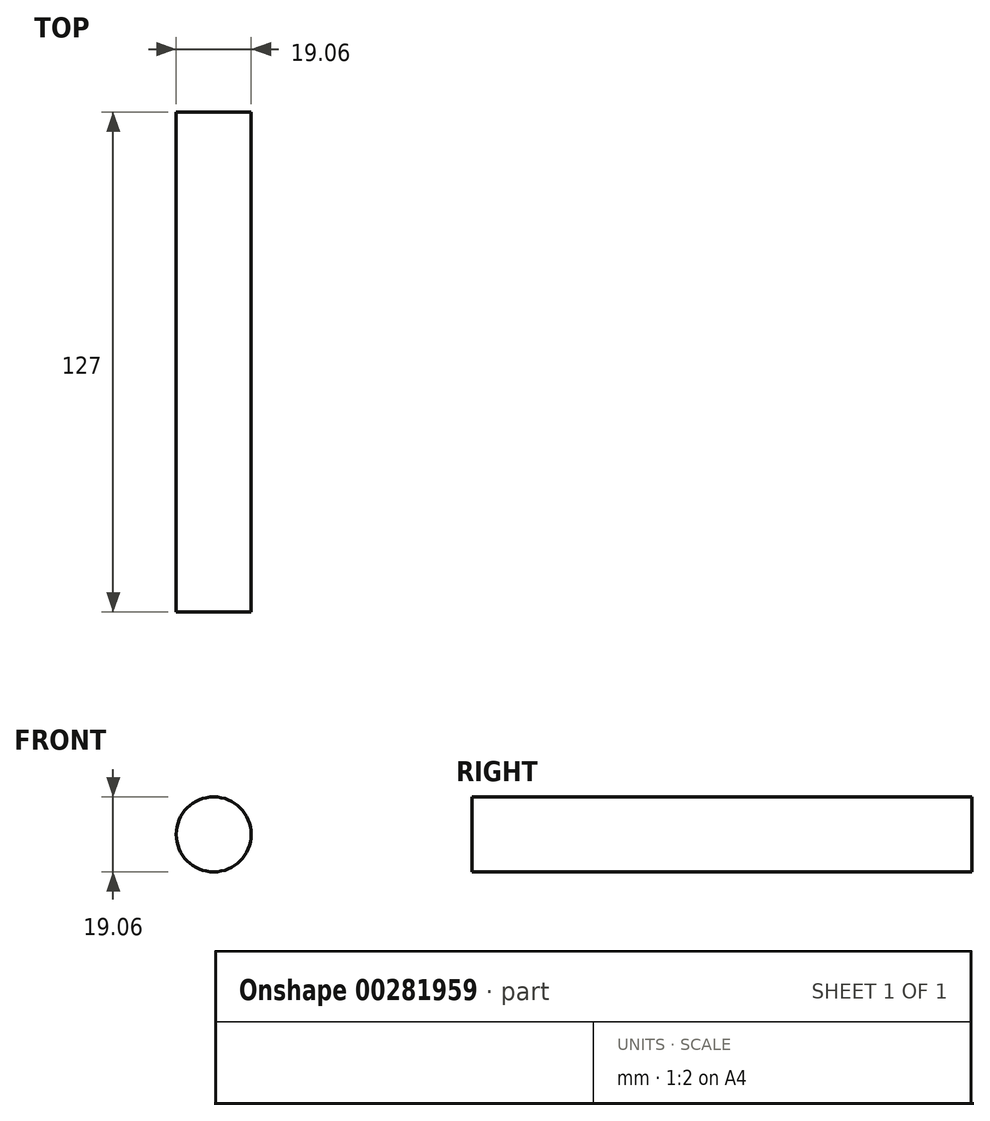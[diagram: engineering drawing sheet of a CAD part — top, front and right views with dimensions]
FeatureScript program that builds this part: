
annotation { "Feature Type Name" : "Feature", "Feature Type Description" : "" }
export const myFeature = defineFeature(function(context is Context, id is Id, definition is map)
    precondition{}
    {
        {
            var Q0;
            Q0=qCreatedBy(makeId("Front.planeOp"),FACE);
            var sketch = newSketch(context, id + "F0", { "sketchPlane" : qUnion([Q0])});
            skCircle(sketch, "E0", {"center": v(0, 0) * mm, "radius": 9.53 * mm});
            skSolve(sketch);
        }
        {
            var Q0;
            Q0=makeQuery(id+"F0.imprint","IMPRINT",FACE,{"disambiguationData":[TD([[makeQuery(id+"F0.imprint","IMPRINT",EDGE,{"derivedFrom":sQuery(id+"F0.wireOp",EDGE,"E0")}),1.0]])]});
            extrude(context, id + "F1", {"entities" : qUnion([Q0]), "depth" : 127 * mm});
        }
    });
